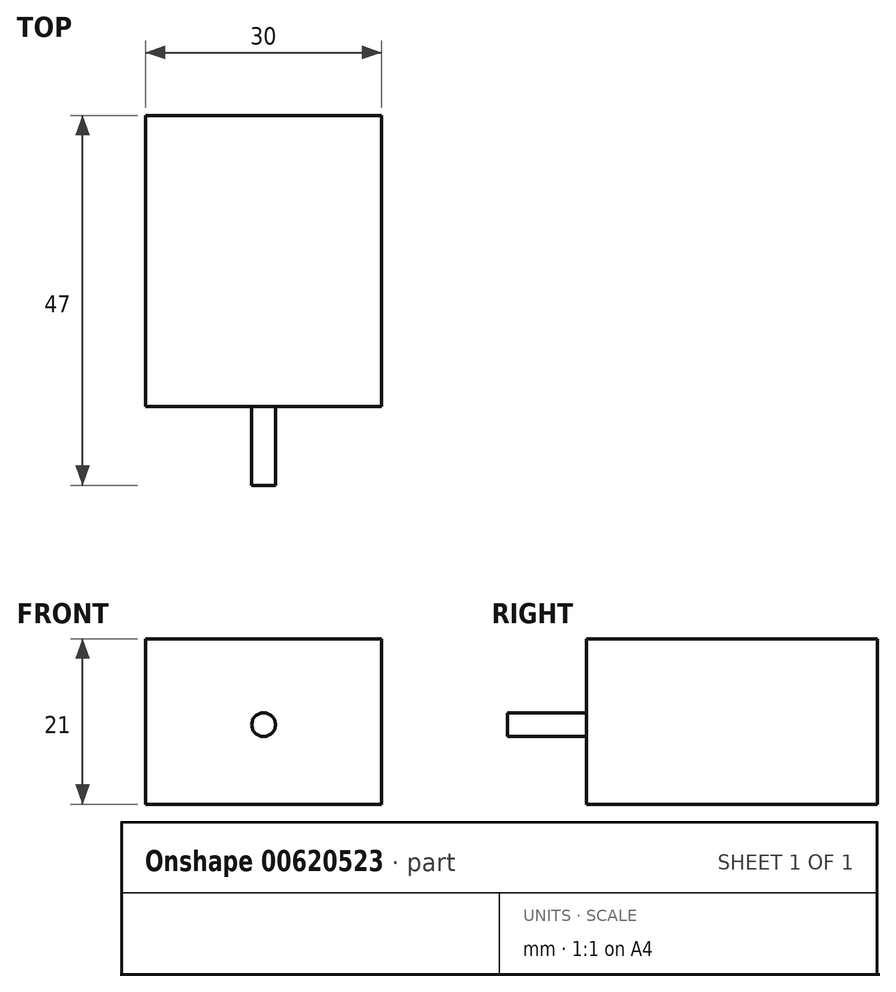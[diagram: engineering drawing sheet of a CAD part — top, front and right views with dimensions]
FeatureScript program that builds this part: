
annotation { "Feature Type Name" : "Feature", "Feature Type Description" : "" }
export const myFeature = defineFeature(function(context is Context, id is Id, definition is map)
    precondition{}
    {
        {
            var Q0;
            Q0=qCreatedBy(makeId("Front.planeOp"),FACE);
            var sketch = newSketch(context, id + "F0", { "sketchPlane" : qUnion([Q0])});
            skLineSegment(sketch, "E0.bottom", {"start": v(-10.98, 9.6) * mm, "end": v(19.02, 9.6) * mm});
            skLineSegment(sketch, "E0.top", {"start": v(-10.98, -11.4) * mm, "end": v(19.02, -11.4) * mm});
            skLineSegment(sketch, "E0.left", {"start": v(-10.98, 9.6) * mm, "end": v(-10.98, -11.4) * mm});
            skLineSegment(sketch, "E0.right", {"start": v(19.02, 9.6) * mm, "end": v(19.02, -11.4) * mm});
            skSolve(sketch);
        }
        {
            var Q0;
            Q0=makeQuery(id+"F0.imprint","IMPRINT",FACE,{"disambiguationData":[TD([[makeQuery(id+"F0.imprint","IMPRINT",EDGE,{"derivedFrom":sQuery(id+"F0.wireOp",EDGE,"E0.bottom")}),-1.0]])]});
            extrude(context, id + "F1", {"entities" : qUnion([Q0]), "depth" : 37 * mm, "offsetDistance" : 25.4 * mm});
        }
        {
            var Q0;
            Q0=makeQuery(id+"F1.opExtrude","CAP_FACE",FACE,{"disambiguationData":[OSD([sQuery(id+"F0.wireOp",EDGE,"E0.bottom"),sQuery(id+"F0.wireOp",EDGE,"E0.top"),sQuery(id+"F0.wireOp",EDGE,"E0.left"),sQuery(id+"F0.wireOp",EDGE,"E0.right")])],"isStart":true});
            var sketch = newSketch(context, id + "F2", { "sketchPlane" : qUnion([Q0])});
            skLineSegment(sketch, "E1.bottom", {"start": v(-14.02, -11.4) * mm, "end": v(-19.02, -11.4) * mm});
            skLineSegment(sketch, "E1.top", {"start": v(-14.02, -6.4) * mm, "end": v(-19.02, -6.4) * mm});
            skLineSegment(sketch, "E1.left", {"start": v(-14.02, -11.4) * mm, "end": v(-14.02, -6.4) * mm});
            skLineSegment(sketch, "E1.right", {"start": v(-19.02, -11.4) * mm, "end": v(-19.02, -6.4) * mm});
            skLineSegment(sketch, "E2.bottom", {"start": v(5.98, -11.4) * mm, "end": v(10.98, -11.4) * mm});
            skLineSegment(sketch, "E2.top", {"start": v(5.98, -6.4) * mm, "end": v(10.98, -6.4) * mm});
            skLineSegment(sketch, "E2.left", {"start": v(5.98, -11.4) * mm, "end": v(5.98, -6.4) * mm});
            skLineSegment(sketch, "E2.right", {"start": v(10.98, -11.4) * mm, "end": v(10.98, -6.4) * mm});
            skSolve(sketch);
        }
        {
            var Q0;
            Q0=makeQuery(id+"F2.imprint","IMPRINT",FACE,{"disambiguationData":[TD([[makeQuery(id+"F2.imprint","IMPRINT",EDGE,{"derivedFrom":sQuery(id+"F2.wireOp",EDGE,"E1.bottom")}),-1.0]])]});
            extrude(context, id + "F3", {"entities" : qUnion([Q0]), "operationType" : NewBodyOperationType.ADD, "oppositeDirection" : true, "depth" : 37 * mm, "offsetDistance" : 25.4 * mm});
        }
        {
            var Q0;
            Q0=makeQuery(id+"F1.opExtrude","CAP_FACE",FACE,{"disambiguationData":[OSD([sQuery(id+"F0.wireOp",EDGE,"E0.bottom"),sQuery(id+"F0.wireOp",EDGE,"E0.top"),sQuery(id+"F0.wireOp",EDGE,"E0.left"),sQuery(id+"F0.wireOp",EDGE,"E0.right")])],"isStart":false});
            var sketch = newSketch(context, id + "F4", { "sketchPlane" : qUnion([Q0])});
            skCircle(sketch, "E3", {"center": v(4.02, -1.3) * mm, "radius": 1.5 * mm});
            skPoint(sketch, "E3.centerSnap0", {"position": v(4.02, -11.4) * mm});
            skSolve(sketch);
        }
        {
            var Q0;
            Q0=makeQuery(id+"F4.imprint","IMPRINT",FACE,{"disambiguationData":[TD([[makeQuery(id+"F4.imprint","IMPRINT",EDGE,{"derivedFrom":sQuery(id+"F4.wireOp",EDGE,"E3")}),1.0]])]});
            extrude(context, id + "F5", {"entities" : qUnion([Q0]), "operationType" : NewBodyOperationType.ADD, "depth" : 10 * mm, "offsetDistance" : 25.4 * mm});
        }
    });
